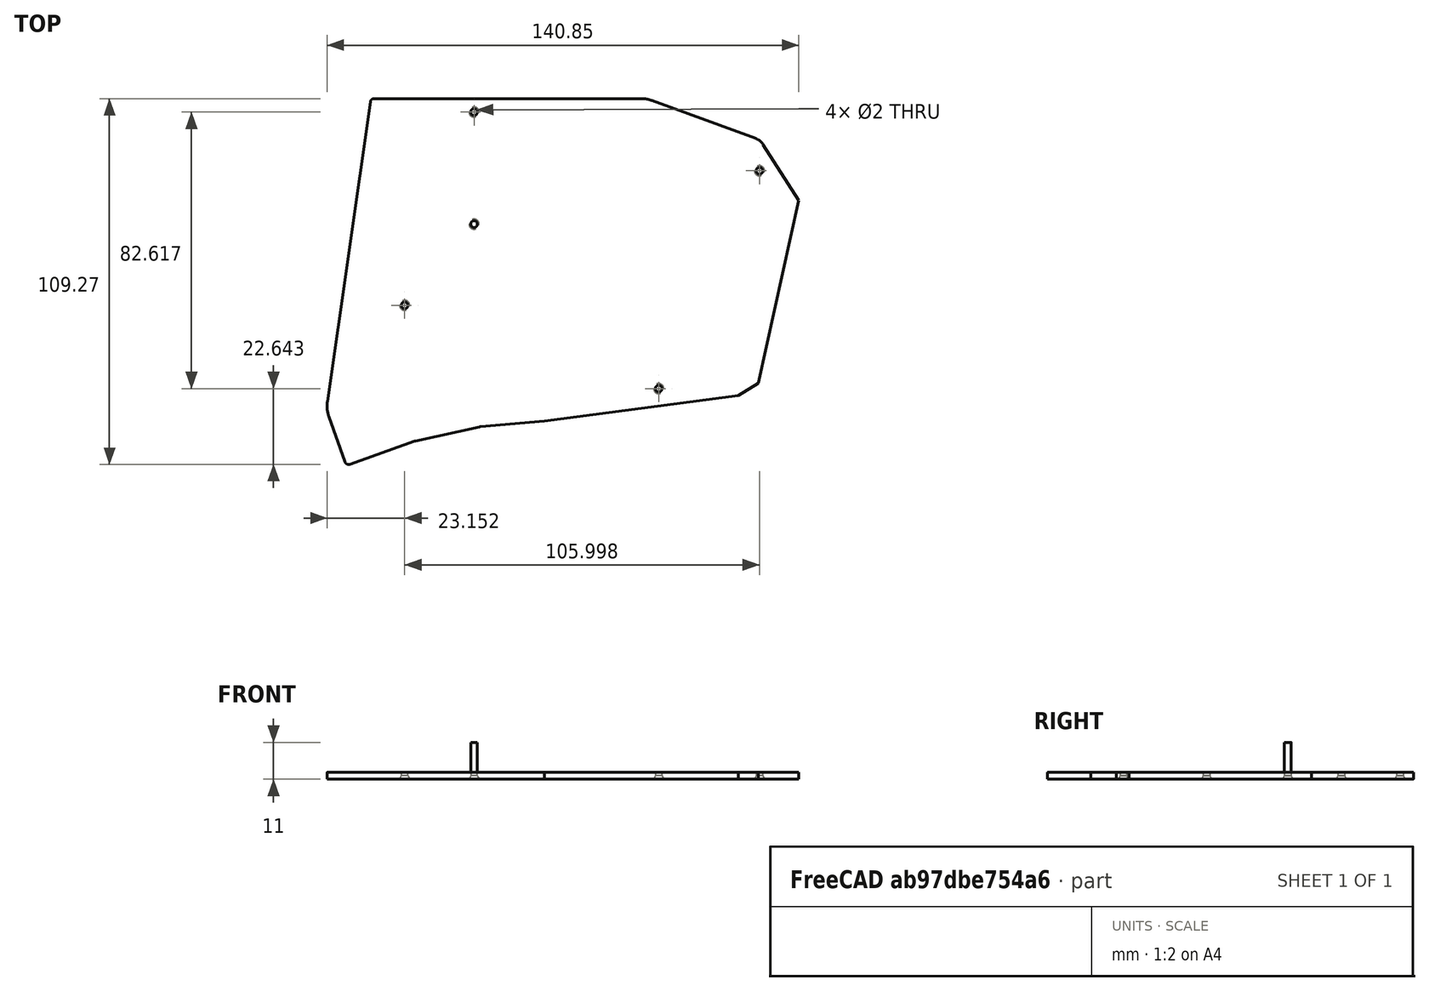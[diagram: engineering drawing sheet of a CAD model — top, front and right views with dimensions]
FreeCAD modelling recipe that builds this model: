
FCSTD DOCUMENT  (FreeCAD 0.21R33668 +26 (Git))
Label: PlateBottom
License: All rights reserved
LicenseURL: http://en.wikipedia.org/wiki/All_rights_reserved
objects: Sketcher::SketchObject×3, PartDesign::Body×2, App::Link×1, PartDesign::SubShapeBinder×1, Part::Offset2D×1, Part::Extrusion×1, PartDesign::AdditiveLoft×1, PartDesign::Pad×1, Part::FeaturePython×1, Part::Cut×1, Part::Refine×1
note: 14 computed .brp shape members not serialized (recipe doc carries the construction recipe); baked Part::Feature solids carry a one-line shape summary decoded from their .brp
EXTERNAL_REF file=KeyColumnArray2.FCStd obj=Body001

FEATURE [App::Link] Link  label="ShellRough"
  LinkedObject = -> <external KeyColumnArray2.FCStd>#Body001
FEATURE [PartDesign::SubShapeBinder] Binder
  BindCopyOnChange = 0
  BindMode = 0
  ClaimChildren = false
  Context = -> Body [Binder.]
  Fuse = false
  MakeFace = true
  OffsetFill = false
  OffsetIntersection = false
  OffsetJoinType = 0
  OffsetOpenResult = false
  PartialLoad = false
  Relative = true
  Support = -> [Link[Thickness.Edge69,Thickness.Edge70,Thickness.Edge86,Thickness.Edge85,Thickness.Edge84,Thickness.Edge83,Thickness.Edge82,Thickness.Edge81]]
  _Version = 2
FEATURE [PartDesign::Body] Body  label="BasePlate"
  Group = -> [Binder]
  Origin = -> Origin
FEATURE [Part::Offset2D] Offset2D
  Fill = false
  Intersection = false
  Join = 0
  Mode = 1
  SelfIntersection = false
  Source = -> Binder
  Value = -0.5
FEATURE [Part::Extrusion] Extrude
  Base = -> Offset2D
  Dir = (0,0,1)
  DirMode = 2
  FaceMakerClass = Part::FaceMakerBullseye
  LengthFwd = 2
  LengthRev = 0
  Solid = false
  Symmetric = false
FEATURE [Sketcher::SketchObject] Sketch
  AttachmentOffset = pos=(0,0,-1) rot=(0,0,1;0rad)
  FullyConstrained = true
  MapMode = 5
  Placement = pos=(0,0,-1) rot=(0,0,1;0rad)
  Support = -> [XY_Plane001]
  sketch-geometry (1):
    g0: Circle CenterX=0 CenterY=0 CenterZ=0 NormalX=0 NormalY=0 NormalZ=1 AngleXU=0 Radius=1
  constraints (2):
    c: Coincident(g0,g-1)
    c: Radius(g0) = 1
FEATURE [Sketcher::SketchObject] Sketch001
  FullyConstrained = true
  MapMode = 5
  Support = -> [XY_Plane001]
  sketch-geometry (1):
    g0: Circle CenterX=0 CenterY=0 CenterZ=0 NormalX=0 NormalY=0 NormalZ=1 AngleXU=0 Radius=1.5
  constraints (2):
    c: Coincident(g0,g-1)
    c: Radius(g0) = 1.5
FEATURE [PartDesign::AdditiveLoft] AdditiveLoft
  Closed = false
  Profile = -> Sketch
  Ruled = false
  Sections = -> [Sketch001]
FEATURE [PartDesign::Pad] Pad
  BaseFeature = -> AdditiveLoft
  Direction = (0,0,-1)
  Length = 10
  Length2 = 10
  Profile = -> AdditiveLoft [Face1]
  Type = 0
FEATURE [PartDesign::Body] Body001  label="ScrewCutter"
  Group = -> [Sketch,Sketch001,AdditiveLoft,Pad]
  Origin = -> Origin001
  Placement = pos=(0,0,0) rot=(1,0,0;3.14159rad)
  Tip = -> Pad
FEATURE [Sketcher::SketchObject] Sketch019
  FullyConstrained = false
  MapMode = 5
  sketch-geometry (4):
    g0: GeomPoint X=-20.7484 Y=-24.2516 Z=0
    g1: GeomPoint X=55.1532 Y=-49.1265 Z=0
    g2: GeomPoint X=85.2491 Y=15.947 Z=0
    g3: GeomPoint X=-0.005864 Y=33.4906 Z=0
FEATURE [Part::FeaturePython] PointArray  # Draft array (typed FeaturePython)
  AlwaysSyncPlacement = false
  Base = -> Body001
  Count = 4
  ExpandArray = false
  PlacementList = 4 placements: [(-20.7484,-24.2516,0),(55.1532,-49.1265,0),(85.2491,15.947,0),(-0.005864,33.4906,0)]
  PointObject = -> Sketch019
  ScaleList = (4) [(1,1,1),(1,1,1),(1,1,1),(1,1,1)]
FEATURE [Part::Cut] Cut
  Base = -> Extrude
  Tool = -> PointArray
FEATURE [Part::Refine] Cut001  label="PlateWithHolesN"
  Source = -> Cut
